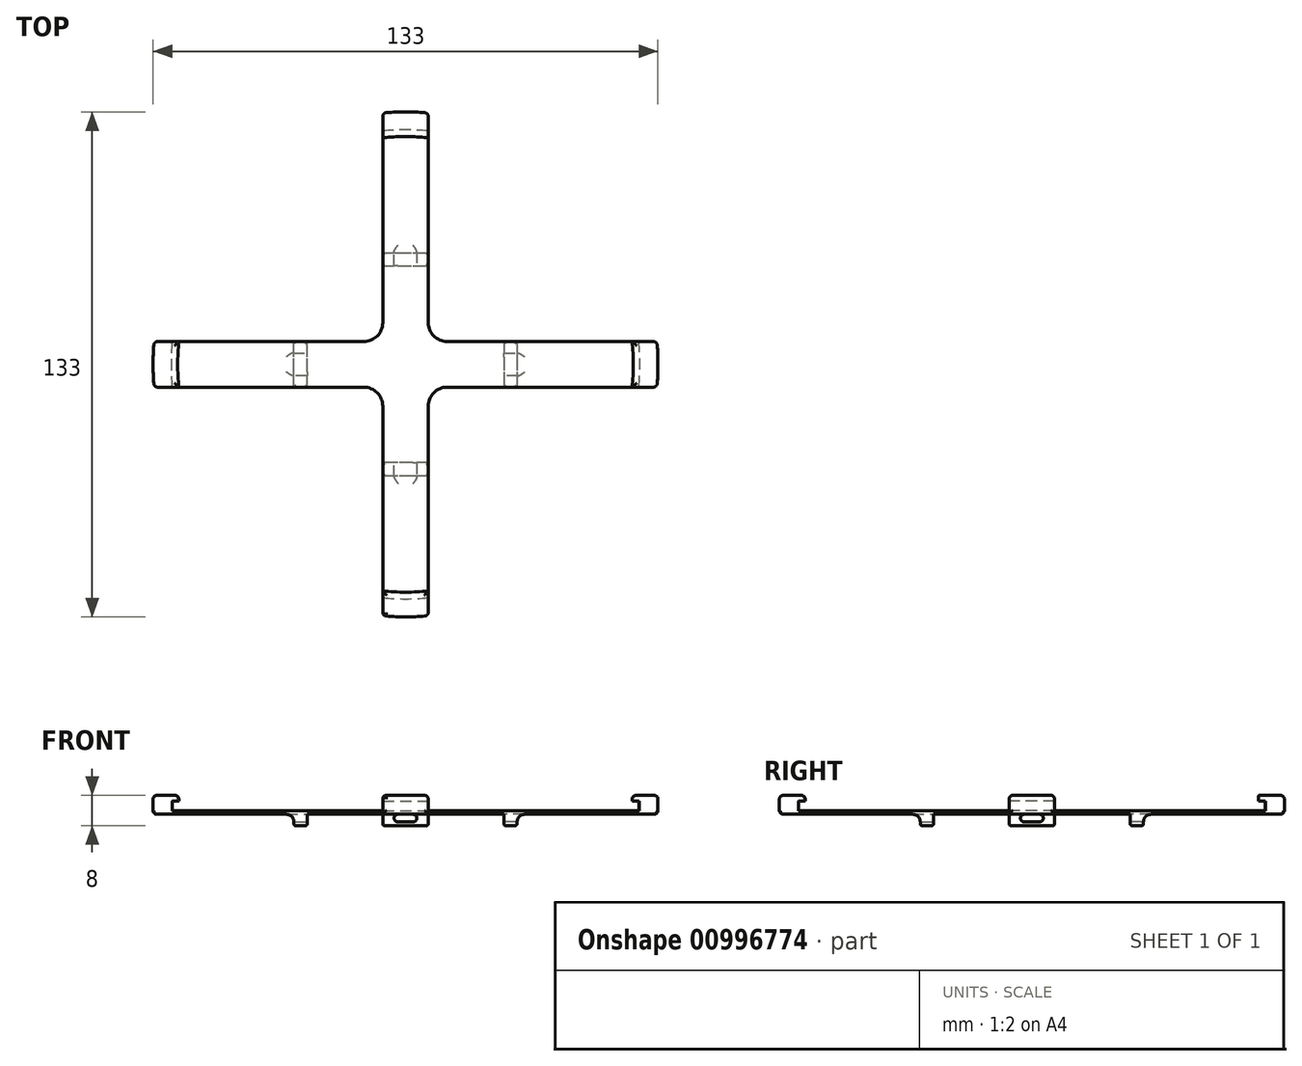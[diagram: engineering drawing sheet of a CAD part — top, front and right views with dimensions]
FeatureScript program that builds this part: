
annotation { "Feature Type Name" : "Feature", "Feature Type Description" : "" }
export const myFeature = defineFeature(function(context is Context, id is Id, definition is map)
    precondition{}
    {
        {
            var Q0;
            Q0=qCreatedBy(makeId("Top.planeOp"),FACE);
            var sketch = newSketch(context, id + "F0", { "sketchPlane" : qUnion([Q0])});
            skCircle(sketch, "E0", {"center": v(0, 0) * mm, "radius": 66.5 * mm, "construction": true});
            skLineSegment(sketch, "E1.bottom", {"start": v(6, -6) * mm, "end": v(-6, -6) * mm, "construction": true});
            skLineSegment(sketch, "E1.top", {"start": v(6, 6) * mm, "end": v(-6, 6) * mm, "construction": true});
            skLineSegment(sketch, "E1.left", {"start": v(6, -6) * mm, "end": v(6, 6) * mm, "construction": true});
            skLineSegment(sketch, "E1.right", {"start": v(-6, -6) * mm, "end": v(-6, 6) * mm, "construction": true});
            skLineSegment(sketch, "E2", {"start": v(-6, 6) * mm, "end": v(-66.23, 6) * mm});
            skLineSegment(sketch, "E3", {"start": v(-6, -6) * mm, "end": v(-66.23, -6) * mm});
            skArc(sketch, "E4", {"start": v(-66.23, 6) * mm, "mid": v(-66.5, 0) * mm, "end": v(-66.23, -6) * mm});
            skLineSegment(sketch, "E5.1.0", {"start": v(-6, -6) * mm, "end": v(-6, -66.23) * mm});
            skLineSegment(sketch, "E5.1.1", {"start": v(6, -6) * mm, "end": v(6, -66.23) * mm});
            skArc(sketch, "E5.1.2", {"start": v(-6, -66.23) * mm, "mid": v(0, -66.5) * mm, "end": v(6, -66.23) * mm});
            skLineSegment(sketch, "E5.2.0", {"start": v(6, -6) * mm, "end": v(66.23, -6) * mm});
            skLineSegment(sketch, "E5.2.1", {"start": v(6, 6) * mm, "end": v(66.23, 6) * mm});
            skArc(sketch, "E5.2.2", {"start": v(66.23, -6) * mm, "mid": v(66.5, 0) * mm, "end": v(66.23, 6) * mm});
            skLineSegment(sketch, "E5.3.0", {"start": v(6, 6) * mm, "end": v(6, 66.23) * mm});
            skLineSegment(sketch, "E5.3.1", {"start": v(-6, 6) * mm, "end": v(-6, 66.23) * mm});
            skArc(sketch, "E5.3.2", {"start": v(6, 66.23) * mm, "mid": v(0, 66.5) * mm, "end": v(-6, 66.23) * mm});
            skSolve(sketch);
        }
        {
            var Q0;
            Q0 = qSketchRegion(id + "F0", true);
            extrude(context, id + "F1", {"entities" : qUnion([Q0]), "depth" : 5 * mm, "offsetDistance" : 25 * mm});
        }
        {
            var Q0;
            Q0=makeQuery(id+"F1.opExtrude","CAP_FACE",FACE,{"disambiguationData":[OSD([sQuery(id+"F0.wireOp",EDGE,"E2"),sQuery(id+"F0.wireOp",EDGE,"E3"),sQuery(id+"F0.wireOp",EDGE,"E4"),sQuery(id+"F0.wireOp",EDGE,"E5.1.0"),sQuery(id+"F0.wireOp",EDGE,"E5.1.1"),sQuery(id+"F0.wireOp",EDGE,"E5.1.2"),sQuery(id+"F0.wireOp",EDGE,"E5.2.0"),sQuery(id+"F0.wireOp",EDGE,"E5.2.1"),sQuery(id+"F0.wireOp",EDGE,"E5.2.2"),sQuery(id+"F0.wireOp",EDGE,"E5.3.0"),sQuery(id+"F0.wireOp",EDGE,"E5.3.1"),sQuery(id+"F0.wireOp",EDGE,"E5.3.2")])],"isStart":false});
            var sketch = newSketch(context, id + "F2", { "sketchPlane" : qUnion([Q0])});
            skCircle(sketch, "E6", {"center": v(0, 0) * mm, "radius": 60 * mm, "construction": true});
            skArc(sketch, "E7", {"start": v(-59.7, 6) * mm, "mid": v(-60, 0) * mm, "end": v(-59.7, -6) * mm});
            skLineSegment(sketch, "E8", {"start": v(-59.7, 6) * mm, "end": v(-6, 6) * mm});
            skLineSegment(sketch, "E9", {"start": v(-59.7, -6) * mm, "end": v(-6, -6) * mm});
            skLineSegment(sketch, "E10.1.0", {"start": v(6, -59.7) * mm, "end": v(6, -6) * mm});
            skArc(sketch, "E10.1.1", {"start": v(-6, -59.7) * mm, "mid": v(0, -60) * mm, "end": v(6, -59.7) * mm});
            skLineSegment(sketch, "E10.1.2", {"start": v(-6, -59.7) * mm, "end": v(-6, -6) * mm});
            skLineSegment(sketch, "E10.2.0", {"start": v(59.7, 6) * mm, "end": v(6, 6) * mm});
            skArc(sketch, "E10.2.1", {"start": v(59.7, -6) * mm, "mid": v(60, 0) * mm, "end": v(59.7, 6) * mm});
            skLineSegment(sketch, "E10.2.2", {"start": v(59.7, -6) * mm, "end": v(6, -6) * mm});
            skLineSegment(sketch, "E10.3.0", {"start": v(-6, 59.7) * mm, "end": v(-6, 6) * mm});
            skArc(sketch, "E10.3.1", {"start": v(6, 59.7) * mm, "mid": v(0, 60) * mm, "end": v(-6, 59.7) * mm});
            skLineSegment(sketch, "E10.3.2", {"start": v(6, 59.7) * mm, "end": v(6, 6) * mm});
            skSolve(sketch);
        }
        {
            var Q0;
            Q0 = qSketchRegion(id + "F2", true);
            extrude(context, id + "F3", {"entities" : qUnion([Q0]), "operationType" : NewBodyOperationType.REMOVE, "oppositeDirection" : true, "depth" : 4 * mm, "offsetDistance" : 25 * mm});
        }
        {
            var Q0;
            Q0=makeQuery(id+"F3.boolean.opBoolean","COPY",FACE,{"derivedFrom":makeQuery(id+"F3.opExtrude","CAP_FACE",FACE,{"disambiguationData":[OSD([sQuery(id+"F2.wireOp",EDGE,"E7"),sQuery(id+"F2.wireOp",EDGE,"E8"),sQuery(id+"F2.wireOp",EDGE,"E9"),sQuery(id+"F2.wireOp",EDGE,"E10.1.0"),sQuery(id+"F2.wireOp",EDGE,"E10.1.1"),sQuery(id+"F2.wireOp",EDGE,"E10.1.2"),sQuery(id+"F2.wireOp",EDGE,"E10.2.0"),sQuery(id+"F2.wireOp",EDGE,"E10.2.1"),sQuery(id+"F2.wireOp",EDGE,"E10.2.2"),sQuery(id+"F2.wireOp",EDGE,"E10.3.0"),sQuery(id+"F2.wireOp",EDGE,"E10.3.1"),sQuery(id+"F2.wireOp",EDGE,"E10.3.2")])],"isStart":false})});
            var sketch = newSketch(context, id + "F4", { "sketchPlane" : qUnion([Q0])});
            skLineSegment(sketch, "E11.bottom", {"start": v(-6, 6) * mm, "end": v(-64.12, 6) * mm, "construction": true});
            skLineSegment(sketch, "E11.top", {"start": v(-6, -6) * mm, "end": v(-64.12, -6) * mm, "construction": true});
            skLineSegment(sketch, "E11.left", {"start": v(-6, 6) * mm, "end": v(-6, -6) * mm, "construction": true});
            skLineSegment(sketch, "E11.right", {"start": v(-64.12, 6) * mm, "end": v(-64.12, -6) * mm, "construction": true});
            skArc(sketch, "E12", {"start": v(-61.46, 6) * mm, "mid": v(-61.75, 0) * mm, "end": v(-61.46, -6) * mm});
            skLineSegment(sketch, "E13", {"start": v(-61.46, 6) * mm, "end": v(-6, 6) * mm});
            skLineSegment(sketch, "E14", {"start": v(-6, -6) * mm, "end": v(-61.46, -6) * mm});
            skLineSegment(sketch, "E15.1.0", {"start": v(6, -6) * mm, "end": v(6, -61.46) * mm});
            skLineSegment(sketch, "E15.1.1", {"start": v(-6, -61.46) * mm, "end": v(-6, -6) * mm});
            skArc(sketch, "E15.1.2", {"start": v(-6, -61.46) * mm, "mid": v(0, -61.75) * mm, "end": v(6, -61.46) * mm});
            skLineSegment(sketch, "E15.2.0", {"start": v(6, 6) * mm, "end": v(61.46, 6) * mm});
            skLineSegment(sketch, "E15.2.1", {"start": v(61.46, -6) * mm, "end": v(6, -6) * mm});
            skArc(sketch, "E15.2.2", {"start": v(61.46, -6) * mm, "mid": v(61.75, 0) * mm, "end": v(61.46, 6) * mm});
            skLineSegment(sketch, "E15.3.0", {"start": v(-6, 6) * mm, "end": v(-6, 61.46) * mm});
            skLineSegment(sketch, "E15.3.1", {"start": v(6, 61.46) * mm, "end": v(6, 6) * mm});
            skArc(sketch, "E15.3.2", {"start": v(6, 61.46) * mm, "mid": v(0, 61.75) * mm, "end": v(-6, 61.46) * mm});
            skPoint(sketch, "E15.center", {"position": v(0, 0) * mm});
            skSolve(sketch);
        }
        {
            var Q0;
            Q0 = qSketchRegion(id + "F4", true);
            extrude(context, id + "F5", {"entities" : qUnion([Q0]), "operationType" : NewBodyOperationType.REMOVE, "depth" : 2.5 * mm, "offsetDistance" : 25 * mm});
        }
        {
            var Q0;
            Q0=makeQuery(id+"F1.opExtrude","SWEPT_EDGE",EDGE,{"disambiguationData":[OSD([sQuery(id+"F0.wireOp",EDGE,"E5.1.1"),sQuery(id+"F0.wireOp",EDGE,"E5.2.0")])]});
            var Q1;
            Q1=makeQuery(id+"F1.opExtrude","SWEPT_EDGE",EDGE,{"disambiguationData":[OSD([sQuery(id+"F0.wireOp",EDGE,"E3"),sQuery(id+"F0.wireOp",EDGE,"E5.1.0")])]});
            var Q2;
            Q2=makeQuery(id+"F1.opExtrude","SWEPT_EDGE",EDGE,{"disambiguationData":[OSD([sQuery(id+"F0.wireOp",EDGE,"E2"),sQuery(id+"F0.wireOp",EDGE,"E5.3.1")])]});
            var Q3;
            Q3=makeQuery(id+"F1.opExtrude","SWEPT_EDGE",EDGE,{"disambiguationData":[OSD([sQuery(id+"F0.wireOp",EDGE,"E5.2.1"),sQuery(id+"F0.wireOp",EDGE,"E5.3.0")])]});
            fillet(context, id + "F6", {"entities" : qUnion([Q0, Q1, Q2, Q3]), "radius" : 5 * mm, "tangentPropagation" : true, "allowEdgeOverflow" : false});
        }
        {
            var Q0;
            Q0=makeQuery(id+"F1.opExtrude","CAP_EDGE",EDGE,{"disambiguationData":[OSD([sQuery(id+"F0.wireOp",EDGE,"E5.3.2")])],"isStart":false});
            var Q1;
            Q1=makeQuery(id+"F3.boolean.opBoolean","COPY",EDGE,{"derivedFrom":makeQuery(id+"F3.opExtrude","CAP_EDGE",EDGE,{"disambiguationData":[OSD([sQuery(id+"F2.wireOp",EDGE,"E10.3.1")])],"isStart":true})});
            var Q2;
            Q2=makeQuery(id+"F1.opExtrude","SWEPT_EDGE",EDGE,{"disambiguationData":[OSD([sQuery(id+"F0.wireOp",EDGE,"E5.3.0"),sQuery(id+"F0.wireOp",EDGE,"E5.3.2")])]});
            var Q3;
            Q3=makeQuery(id+"F1.opExtrude","CAP_EDGE",EDGE,{"disambiguationData":[OSD([sQuery(id+"F0.wireOp",EDGE,"E5.3.0")])],"isStart":false});
            var Q4;
            Q4=makeQuery(id+"F1.opExtrude","CAP_EDGE",EDGE,{"disambiguationData":[OSD([sQuery(id+"F0.wireOp",EDGE,"E5.3.1")])],"isStart":false});
            var Q5;
            Q5=makeQuery(id+"F1.opExtrude","SWEPT_EDGE",EDGE,{"disambiguationData":[OSD([sQuery(id+"F0.wireOp",EDGE,"E5.3.1"),sQuery(id+"F0.wireOp",EDGE,"E5.3.2")])]});
            var Q6;
            Q6=makeQuery(id+"F1.opExtrude","CAP_EDGE",EDGE,{"disambiguationData":[OSD([sQuery(id+"F0.wireOp",EDGE,"E5.3.2")])],"isStart":true});
            var Q7;
            Q7=makeQuery(id+"F1.opExtrude","CAP_EDGE",EDGE,{"disambiguationData":[OSD([sQuery(id+"F0.wireOp",EDGE,"E2")])],"isStart":false});
            var Q8;
            Q8=makeQuery(id+"F3.boolean.opBoolean","COPY",EDGE,{"derivedFrom":makeQuery(id+"F3.opExtrude","CAP_EDGE",EDGE,{"disambiguationData":[OSD([sQuery(id+"F2.wireOp",EDGE,"E7")])],"isStart":true})});
            var Q9;
            Q9=makeQuery(id+"F1.opExtrude","CAP_EDGE",EDGE,{"disambiguationData":[OSD([sQuery(id+"F0.wireOp",EDGE,"E3")])],"isStart":false});
            var Q10;
            Q10=makeQuery(id+"F1.opExtrude","CAP_EDGE",EDGE,{"disambiguationData":[OSD([sQuery(id+"F0.wireOp",EDGE,"E4")])],"isStart":false});
            var Q11;
            Q11=makeQuery(id+"F1.opExtrude","SWEPT_EDGE",EDGE,{"disambiguationData":[OSD([sQuery(id+"F0.wireOp",EDGE,"E3"),sQuery(id+"F0.wireOp",EDGE,"E4")])]});
            var Q12;
            Q12=makeQuery(id+"F1.opExtrude","SWEPT_EDGE",EDGE,{"disambiguationData":[OSD([sQuery(id+"F0.wireOp",EDGE,"E2"),sQuery(id+"F0.wireOp",EDGE,"E4")])]});
            var Q13;
            Q13=makeQuery(id+"F1.opExtrude","SWEPT_EDGE",EDGE,{"disambiguationData":[OSD([sQuery(id+"F0.wireOp",EDGE,"E5.1.0"),sQuery(id+"F0.wireOp",EDGE,"E5.1.2")])]});
            var Q14;
            Q14=makeQuery(id+"F1.opExtrude","CAP_EDGE",EDGE,{"disambiguationData":[OSD([sQuery(id+"F0.wireOp",EDGE,"E5.1.2")])],"isStart":false});
            var Q15;
            Q15=makeQuery(id+"F1.opExtrude","SWEPT_EDGE",EDGE,{"disambiguationData":[OSD([sQuery(id+"F0.wireOp",EDGE,"E5.1.1"),sQuery(id+"F0.wireOp",EDGE,"E5.1.2")])]});
            var Q16;
            Q16=makeQuery(id+"F3.boolean.opBoolean","COPY",EDGE,{"derivedFrom":makeQuery(id+"F3.opExtrude","CAP_EDGE",EDGE,{"disambiguationData":[OSD([sQuery(id+"F2.wireOp",EDGE,"E10.1.1")])],"isStart":true})});
            var Q17;
            Q17=makeQuery(id+"F1.opExtrude","CAP_EDGE",EDGE,{"disambiguationData":[OSD([sQuery(id+"F0.wireOp",EDGE,"E5.1.1")])],"isStart":false});
            var Q18;
            Q18=makeQuery(id+"F1.opExtrude","CAP_EDGE",EDGE,{"disambiguationData":[OSD([sQuery(id+"F0.wireOp",EDGE,"E5.1.0")])],"isStart":false});
            var Q19;
            Q19=makeQuery(id+"F1.opExtrude","SWEPT_EDGE",EDGE,{"disambiguationData":[OSD([sQuery(id+"F0.wireOp",EDGE,"E5.2.1"),sQuery(id+"F0.wireOp",EDGE,"E5.2.2")])]});
            var Q20;
            Q20=makeQuery(id+"F1.opExtrude","CAP_EDGE",EDGE,{"disambiguationData":[OSD([sQuery(id+"F0.wireOp",EDGE,"E5.2.2")])],"isStart":true});
            var Q21;
            Q21=makeQuery(id+"F1.opExtrude","CAP_EDGE",EDGE,{"disambiguationData":[OSD([sQuery(id+"F0.wireOp",EDGE,"E5.2.2")])],"isStart":false});
            var Q22;
            Q22=makeQuery(id+"F1.opExtrude","SWEPT_EDGE",EDGE,{"disambiguationData":[OSD([sQuery(id+"F0.wireOp",EDGE,"E5.2.0"),sQuery(id+"F0.wireOp",EDGE,"E5.2.2")])]});
            var Q23;
            Q23=makeQuery(id+"F1.opExtrude","CAP_EDGE",EDGE,{"disambiguationData":[OSD([sQuery(id+"F0.wireOp",EDGE,"E5.2.1")])],"isStart":false});
            var Q24;
            Q24=makeQuery(id+"F3.boolean.opBoolean","COPY",EDGE,{"derivedFrom":makeQuery(id+"F3.opExtrude","CAP_EDGE",EDGE,{"disambiguationData":[OSD([sQuery(id+"F2.wireOp",EDGE,"E10.2.1")])],"isStart":true})});
            var Q25;
            Q25=makeQuery(id+"F1.opExtrude","CAP_EDGE",EDGE,{"disambiguationData":[OSD([sQuery(id+"F0.wireOp",EDGE,"E5.2.0")])],"isStart":false});
            var Q26;
            Q26=makeQuery(id+"F1.opExtrude","CAP_EDGE",EDGE,{"disambiguationData":[OSD([sQuery(id+"F0.wireOp",EDGE,"E4")])],"isStart":true});
            var Q27;
            Q27=makeQuery(id+"F1.opExtrude","CAP_EDGE",EDGE,{"disambiguationData":[OSD([sQuery(id+"F0.wireOp",EDGE,"E5.1.2")])],"isStart":true});
            fillet(context, id + "F7", {"entities" : qUnion([Q0, Q1, Q2, Q3, Q4, Q5, Q6, Q7, Q8, Q9, Q10, Q11, Q12, Q13, Q14, Q15, Q16, Q17, Q18, Q19, Q20, Q21, Q22, Q23, Q24, Q25, Q26, Q27]), "radius" : 1 * mm, "tangentPropagation" : true, "allowEdgeOverflow" : false});
        }
        {
            var Q0;
            Q0=makeQuery(id+"F1.opExtrude","CAP_FACE",FACE,{"disambiguationData":[OSD([sQuery(id+"F0.wireOp",EDGE,"E2"),sQuery(id+"F0.wireOp",EDGE,"E3"),sQuery(id+"F0.wireOp",EDGE,"E4"),sQuery(id+"F0.wireOp",EDGE,"E5.1.0"),sQuery(id+"F0.wireOp",EDGE,"E5.1.1"),sQuery(id+"F0.wireOp",EDGE,"E5.1.2"),sQuery(id+"F0.wireOp",EDGE,"E5.2.0"),sQuery(id+"F0.wireOp",EDGE,"E5.2.1"),sQuery(id+"F0.wireOp",EDGE,"E5.2.2"),sQuery(id+"F0.wireOp",EDGE,"E5.3.0"),sQuery(id+"F0.wireOp",EDGE,"E5.3.1"),sQuery(id+"F0.wireOp",EDGE,"E5.3.2")])],"isStart":true});
            var sketch = newSketch(context, id + "F8", { "sketchPlane" : qUnion([Q0])});
            skCircle(sketch, "E16", {"center": v(0, 0) * mm, "radius": 30 * mm, "construction": true});
            skLineSegment(sketch, "E17", {"start": v(0, 0) * mm, "end": v(-65.5, 0) * mm, "construction": true});
            skLineSegment(sketch, "E18.bottom", {"start": v(-29.4, 6) * mm, "end": v(-25.9, 6) * mm});
            skLineSegment(sketch, "E18.top", {"start": v(-29.4, -6) * mm, "end": v(-25.9, -6) * mm});
            skLineSegment(sketch, "E18.left", {"start": v(-29.4, 6) * mm, "end": v(-29.4, -6) * mm});
            skLineSegment(sketch, "E18.right", {"start": v(-25.9, 6) * mm, "end": v(-25.9, -6) * mm});
            skLineSegment(sketch, "E19.1.0", {"start": v(-6, -29.4) * mm, "end": v(-6, -25.9) * mm});
            skLineSegment(sketch, "E19.1.1", {"start": v(-6, -25.9) * mm, "end": v(6, -25.9) * mm});
            skLineSegment(sketch, "E19.1.2", {"start": v(6, -29.4) * mm, "end": v(6, -25.9) * mm});
            skLineSegment(sketch, "E19.1.3", {"start": v(-6, -29.4) * mm, "end": v(6, -29.4) * mm});
            skLineSegment(sketch, "E19.2.0", {"start": v(29.4, -6) * mm, "end": v(25.9, -6) * mm});
            skLineSegment(sketch, "E19.2.1", {"start": v(25.9, -6) * mm, "end": v(25.9, 6) * mm});
            skLineSegment(sketch, "E19.2.2", {"start": v(29.4, 6) * mm, "end": v(25.9, 6) * mm});
            skLineSegment(sketch, "E19.2.3", {"start": v(29.4, -6) * mm, "end": v(29.4, 6) * mm});
            skLineSegment(sketch, "E19.3.0", {"start": v(6, 29.4) * mm, "end": v(6, 25.9) * mm});
            skLineSegment(sketch, "E19.3.1", {"start": v(6, 25.9) * mm, "end": v(-6, 25.9) * mm});
            skLineSegment(sketch, "E19.3.2", {"start": v(-6, 29.4) * mm, "end": v(-6, 25.9) * mm});
            skLineSegment(sketch, "E19.3.3", {"start": v(6, 29.4) * mm, "end": v(-6, 29.4) * mm});
            skSolve(sketch);
        }
        {
            var Q0;
            Q0 = qSketchRegion(id + "F8", true);
            extrude(context, id + "F9", {"entities" : qUnion([Q0]), "operationType" : NewBodyOperationType.ADD, "depth" : 3 * mm, "offsetDistance" : 25 * mm});
        }
        {
            var Q0;
            {var subQ0=sQuery(id+"F0.wireOp",EDGE,"E5.3.0");var subQ1=sQuery(id+"F0.wireOp",EDGE,"E5.2.1");var subQ2=sQuery(id+"F0.wireOp",EDGE,"E5.2.0");var subQ3=sQuery(id+"F0.wireOp",EDGE,"E5.1.1");var subQ4=sQuery(id+"F0.wireOp",EDGE,"E5.1.0");var subQ5=sQuery(id+"F0.wireOp",EDGE,"E3");var subQ6=sQuery(id+"F0.wireOp",EDGE,"E2");var subQ7=sQuery(id+"F0.wireOp",EDGE,"E5.3.1");Q0=makeQuery(id+"F9.boolean.opBoolean","SPLIT",FACE,{"disambiguationData":[TD([makeQuery(id+"F9.opExtrude","SWEPT_FACE",FACE,{"disambiguationData":[OSD([sQuery(id+"F8.wireOp",EDGE,"E18.right")])]})])],"derivedFrom":makeQuery(id+"F1.opExtrude","CAP_FACE",FACE,{"disambiguationData":[OSD([subQ6,subQ5,sQuery(id+"F0.wireOp",EDGE,"E4"),subQ4,subQ3,sQuery(id+"F0.wireOp",EDGE,"E5.1.2"),subQ2,subQ1,sQuery(id+"F0.wireOp",EDGE,"E5.2.2"),subQ0,subQ7,sQuery(id+"F0.wireOp",EDGE,"E5.3.2")])],"isStart":true})});}
            var sketch = newSketch(context, id + "F10", { "sketchPlane" : qUnion([Q0])});
            skLineSegment(sketch, "E20", {"start": v(0, 0) * mm, "end": v(-61.83, 0) * mm, "construction": true});
            skLineSegment(sketch, "E21.0", {"start": v(0, 3) * mm, "end": v(-61.83, 3) * mm, "construction": true});
            skLineSegment(sketch, "E22.0", {"start": v(0, -3) * mm, "end": v(-61.83, -3) * mm, "construction": true});
            skLineSegment(sketch, "E23.bottom", {"start": v(-30.91, 3) * mm, "end": v(-23.73, 3) * mm});
            skLineSegment(sketch, "E23.top", {"start": v(-30.91, -3) * mm, "end": v(-23.73, -3) * mm});
            skLineSegment(sketch, "E23.left", {"start": v(-30.91, 3) * mm, "end": v(-30.91, -3) * mm});
            skLineSegment(sketch, "E23.right", {"start": v(-23.73, 3) * mm, "end": v(-23.73, -3) * mm});
            skLineSegment(sketch, "E24.1.0", {"start": v(-3, -30.91) * mm, "end": v(-3, -23.73) * mm});
            skLineSegment(sketch, "E24.1.1", {"start": v(3, -30.91) * mm, "end": v(3, -23.73) * mm});
            skLineSegment(sketch, "E24.1.2", {"start": v(-3, -23.73) * mm, "end": v(3, -23.73) * mm});
            skLineSegment(sketch, "E24.1.3", {"start": v(-3, -30.91) * mm, "end": v(3, -30.91) * mm});
            skLineSegment(sketch, "E24.2.0", {"start": v(30.91, -3) * mm, "end": v(23.73, -3) * mm});
            skLineSegment(sketch, "E24.2.1", {"start": v(30.91, 3) * mm, "end": v(23.73, 3) * mm});
            skLineSegment(sketch, "E24.2.2", {"start": v(23.73, -3) * mm, "end": v(23.73, 3) * mm});
            skLineSegment(sketch, "E24.2.3", {"start": v(30.91, -3) * mm, "end": v(30.91, 3) * mm});
            skLineSegment(sketch, "E24.3.0", {"start": v(3, 30.91) * mm, "end": v(3, 23.73) * mm});
            skLineSegment(sketch, "E24.3.1", {"start": v(-3, 30.91) * mm, "end": v(-3, 23.73) * mm});
            skLineSegment(sketch, "E24.3.2", {"start": v(3, 23.73) * mm, "end": v(-3, 23.73) * mm});
            skLineSegment(sketch, "E24.3.3", {"start": v(3, 30.91) * mm, "end": v(-3, 30.91) * mm});
            skPoint(sketch, "E24.center", {"position": v(0, 0) * mm});
            skSolve(sketch);
        }
        {
            var Q0;
            Q0 = qSketchRegion(id + "F10", true);
            extrude(context, id + "F11", {"entities" : qUnion([Q0]), "operationType" : NewBodyOperationType.REMOVE, "depth" : 2 * mm, "offsetDistance" : 25 * mm});
        }
        {
            var Q0;
            {var subQ0=sQuery(id+"F8.wireOp",EDGE,"E18.left");var subQ1=sQuery(id+"F0.wireOp",EDGE,"E3");Q0=makeQuery(id+"F11.boolean.opBoolean","SPLIT",EDGE,{"disambiguationData":[TD([makeQuery(id+"F1.opExtrude","SWEPT_FACE",FACE,{"disambiguationData":[OSD([subQ1])]})])],"derivedFrom":makeQuery(id+"F9.opExtrude","CAP_EDGE",EDGE,{"disambiguationData":[OSD([subQ0])],"isStart":true})});}
            var Q1;
            {var subQ0=sQuery(id+"F8.wireOp",EDGE,"E18.left");var subQ1=sQuery(id+"F0.wireOp",EDGE,"E2");Q1=makeQuery(id+"F11.boolean.opBoolean","SPLIT",EDGE,{"disambiguationData":[TD([makeQuery(id+"F1.opExtrude","SWEPT_FACE",FACE,{"disambiguationData":[OSD([subQ1])]})])],"derivedFrom":makeQuery(id+"F9.opExtrude","CAP_EDGE",EDGE,{"disambiguationData":[OSD([subQ0])],"isStart":true})});}
            var Q2;
            {var subQ0=sQuery(id+"F0.wireOp",EDGE,"E2");var subQ1=sQuery(id+"F8.wireOp",EDGE,"E18.right");Q2=makeQuery(id+"F11.boolean.opBoolean","SPLIT",EDGE,{"disambiguationData":[TD([makeQuery(id+"F1.opExtrude","SWEPT_FACE",FACE,{"disambiguationData":[OSD([subQ0])]})])],"derivedFrom":makeQuery(id+"F9.opExtrude","CAP_EDGE",EDGE,{"disambiguationData":[OSD([subQ1])],"isStart":true})});}
            var Q3;
            {var subQ0=sQuery(id+"F8.wireOp",EDGE,"E18.right");var subQ2=sQuery(id+"F0.wireOp",EDGE,"E3");Q3=makeQuery(id+"F11.boolean.opBoolean","SPLIT",EDGE,{"disambiguationData":[TD([makeQuery(id+"F1.opExtrude","SWEPT_FACE",FACE,{"disambiguationData":[OSD([subQ2])]})])],"derivedFrom":makeQuery(id+"F9.opExtrude","CAP_EDGE",EDGE,{"disambiguationData":[OSD([subQ0])],"isStart":true})});}
            var Q4;
            {var subQ0=sQuery(id+"F8.wireOp",EDGE,"E19.2.3");var subQ2=sQuery(id+"F0.wireOp",EDGE,"E5.2.1");Q4=makeQuery(id+"F11.boolean.opBoolean","SPLIT",EDGE,{"disambiguationData":[TD([makeQuery(id+"F1.opExtrude","SWEPT_FACE",FACE,{"disambiguationData":[OSD([subQ2])]})])],"derivedFrom":makeQuery(id+"F9.opExtrude","CAP_EDGE",EDGE,{"disambiguationData":[OSD([subQ0])],"isStart":true})});}
            var Q5;
            {var subQ0=sQuery(id+"F8.wireOp",EDGE,"E19.2.3");var subQ1=sQuery(id+"F0.wireOp",EDGE,"E5.2.0");Q5=makeQuery(id+"F11.boolean.opBoolean","SPLIT",EDGE,{"disambiguationData":[TD([makeQuery(id+"F1.opExtrude","SWEPT_FACE",FACE,{"disambiguationData":[OSD([subQ1])]})])],"derivedFrom":makeQuery(id+"F9.opExtrude","CAP_EDGE",EDGE,{"disambiguationData":[OSD([subQ0])],"isStart":true})});}
            var Q6;
            {var subQ0=sQuery(id+"F8.wireOp",EDGE,"E19.2.1");var subQ1=sQuery(id+"F0.wireOp",EDGE,"E5.2.1");Q6=makeQuery(id+"F11.boolean.opBoolean","SPLIT",EDGE,{"disambiguationData":[TD([makeQuery(id+"F1.opExtrude","SWEPT_FACE",FACE,{"disambiguationData":[OSD([subQ1])]})])],"derivedFrom":makeQuery(id+"F9.opExtrude","CAP_EDGE",EDGE,{"disambiguationData":[OSD([subQ0])],"isStart":true})});}
            var Q7;
            {var subQ0=sQuery(id+"F8.wireOp",EDGE,"E19.2.1");var subQ1=sQuery(id+"F0.wireOp",EDGE,"E5.2.0");Q7=makeQuery(id+"F11.boolean.opBoolean","SPLIT",EDGE,{"disambiguationData":[TD([makeQuery(id+"F1.opExtrude","SWEPT_FACE",FACE,{"disambiguationData":[OSD([subQ1])]})])],"derivedFrom":makeQuery(id+"F9.opExtrude","CAP_EDGE",EDGE,{"disambiguationData":[OSD([subQ0])],"isStart":true})});}
            var Q8;
            {var subQ0=sQuery(id+"F0.wireOp",EDGE,"E5.1.1");var subQ1=sQuery(id+"F8.wireOp",EDGE,"E19.3.1");Q8=makeQuery(id+"F11.boolean.opBoolean","SPLIT",EDGE,{"disambiguationData":[TD([makeQuery(id+"F1.opExtrude","SWEPT_FACE",FACE,{"disambiguationData":[OSD([subQ0])]})])],"derivedFrom":makeQuery(id+"F9.opExtrude","CAP_EDGE",EDGE,{"disambiguationData":[OSD([subQ1])],"isStart":true})});}
            var Q9;
            {var subQ0=sQuery(id+"F0.wireOp",EDGE,"E5.1.0");var subQ1=sQuery(id+"F8.wireOp",EDGE,"E19.3.1");Q9=makeQuery(id+"F11.boolean.opBoolean","SPLIT",EDGE,{"disambiguationData":[TD([makeQuery(id+"F1.opExtrude","SWEPT_FACE",FACE,{"disambiguationData":[OSD([subQ0])]})])],"derivedFrom":makeQuery(id+"F9.opExtrude","CAP_EDGE",EDGE,{"disambiguationData":[OSD([subQ1])],"isStart":true})});}
            var Q10;
            {var subQ0=sQuery(id+"F0.wireOp",EDGE,"E5.3.1");var subQ1=sQuery(id+"F8.wireOp",EDGE,"E19.1.3");Q10=makeQuery(id+"F11.boolean.opBoolean","SPLIT",EDGE,{"disambiguationData":[TD([makeQuery(id+"F1.opExtrude","SWEPT_FACE",FACE,{"disambiguationData":[OSD([subQ0])]})])],"derivedFrom":makeQuery(id+"F9.opExtrude","CAP_EDGE",EDGE,{"disambiguationData":[OSD([subQ1])],"isStart":true})});}
            var Q11;
            {var subQ0=sQuery(id+"F8.wireOp",EDGE,"E19.1.3");var subQ1=sQuery(id+"F0.wireOp",EDGE,"E5.3.0");Q11=makeQuery(id+"F11.boolean.opBoolean","SPLIT",EDGE,{"disambiguationData":[TD([makeQuery(id+"F1.opExtrude","SWEPT_FACE",FACE,{"disambiguationData":[OSD([subQ1])]})])],"derivedFrom":makeQuery(id+"F9.opExtrude","CAP_EDGE",EDGE,{"disambiguationData":[OSD([subQ0])],"isStart":true})});}
            var Q12;
            {var subQ0=sQuery(id+"F8.wireOp",EDGE,"E19.1.1");var subQ1=sQuery(id+"F0.wireOp",EDGE,"E5.3.0");Q12=makeQuery(id+"F11.boolean.opBoolean","SPLIT",EDGE,{"disambiguationData":[TD([makeQuery(id+"F1.opExtrude","SWEPT_FACE",FACE,{"disambiguationData":[OSD([subQ1])]})])],"derivedFrom":makeQuery(id+"F9.opExtrude","CAP_EDGE",EDGE,{"disambiguationData":[OSD([subQ0])],"isStart":true})});}
            var Q13;
            {var subQ0=sQuery(id+"F8.wireOp",EDGE,"E19.1.1");var subQ1=sQuery(id+"F0.wireOp",EDGE,"E5.3.1");Q13=makeQuery(id+"F11.boolean.opBoolean","SPLIT",EDGE,{"disambiguationData":[TD([makeQuery(id+"F1.opExtrude","SWEPT_FACE",FACE,{"disambiguationData":[OSD([subQ1])]})])],"derivedFrom":makeQuery(id+"F9.opExtrude","CAP_EDGE",EDGE,{"disambiguationData":[OSD([subQ0])],"isStart":true})});}
            var Q14;
            {var subQ0=sQuery(id+"F8.wireOp",EDGE,"E19.3.3");var subQ1=sQuery(id+"F0.wireOp",EDGE,"E5.1.1");Q14=makeQuery(id+"F11.boolean.opBoolean","SPLIT",EDGE,{"disambiguationData":[TD([makeQuery(id+"F1.opExtrude","SWEPT_FACE",FACE,{"disambiguationData":[OSD([subQ1])]})])],"derivedFrom":makeQuery(id+"F9.opExtrude","CAP_EDGE",EDGE,{"disambiguationData":[OSD([subQ0])],"isStart":true})});}
            var Q15;
            {var subQ0=sQuery(id+"F8.wireOp",EDGE,"E19.3.3");var subQ1=sQuery(id+"F0.wireOp",EDGE,"E5.1.0");Q15=makeQuery(id+"F11.boolean.opBoolean","SPLIT",EDGE,{"disambiguationData":[TD([makeQuery(id+"F1.opExtrude","SWEPT_FACE",FACE,{"disambiguationData":[OSD([subQ1])]})])],"derivedFrom":makeQuery(id+"F9.opExtrude","CAP_EDGE",EDGE,{"disambiguationData":[OSD([subQ0])],"isStart":true})});}
            fillet(context, id + "F12", {"entities" : qUnion([Q0, Q1, Q2, Q3, Q4, Q5, Q6, Q7, Q8, Q9, Q10, Q11, Q12, Q13, Q14, Q15]), "radius" : 2 * mm, "tangentPropagation" : true, "allowEdgeOverflow" : false});
        }
        {
            var Q0;
            Q0=makeQuery(id+"F9.opExtrude","CAP_FACE",FACE,{"disambiguationData":[OSD([sQuery(id+"F8.wireOp",EDGE,"E18.bottom"),sQuery(id+"F8.wireOp",EDGE,"E18.top"),sQuery(id+"F8.wireOp",EDGE,"E18.left"),sQuery(id+"F8.wireOp",EDGE,"E18.right")])],"isStart":false});
            var Q1;
            Q1=makeQuery(id+"F9.opExtrude","CAP_FACE",FACE,{"disambiguationData":[OSD([sQuery(id+"F8.wireOp",EDGE,"E19.3.0"),sQuery(id+"F8.wireOp",EDGE,"E19.3.1"),sQuery(id+"F8.wireOp",EDGE,"E19.3.2"),sQuery(id+"F8.wireOp",EDGE,"E19.3.3")])],"isStart":false});
            var Q2;
            Q2=makeQuery(id+"F9.opExtrude","CAP_FACE",FACE,{"disambiguationData":[OSD([sQuery(id+"F8.wireOp",EDGE,"E19.2.0"),sQuery(id+"F8.wireOp",EDGE,"E19.2.1"),sQuery(id+"F8.wireOp",EDGE,"E19.2.2"),sQuery(id+"F8.wireOp",EDGE,"E19.2.3")])],"isStart":false});
            var Q3;
            Q3=makeQuery(id+"F9.opExtrude","CAP_FACE",FACE,{"disambiguationData":[OSD([sQuery(id+"F8.wireOp",EDGE,"E19.1.0"),sQuery(id+"F8.wireOp",EDGE,"E19.1.1"),sQuery(id+"F8.wireOp",EDGE,"E19.1.2"),sQuery(id+"F8.wireOp",EDGE,"E19.1.3")])],"isStart":false});
            fillet(context, id + "F13", {"entities" : qUnion([Q0, Q1, Q2, Q3]), "radius" : 0.5 * mm, "tangentPropagation" : true, "allowEdgeOverflow" : false});
        }
        {
            var Q0;
            Q0=makeQuery(id+"F11.boolean.opBoolean","COPY",EDGE,{"derivedFrom":makeQuery(id+"F11.opExtrude","CAP_EDGE",EDGE,{"disambiguationData":[OSD([sQuery(id+"F10.wireOp",EDGE,"E24.1.0")])],"isStart":false})});
            var Q1;
            Q1=makeQuery(id+"F11.boolean.opBoolean","COPY",EDGE,{"derivedFrom":makeQuery(id+"F11.opExtrude","CAP_EDGE",EDGE,{"disambiguationData":[OSD([sQuery(id+"F10.wireOp",EDGE,"E23.bottom")])],"isStart":false})});
            var Q2;
            Q2=makeQuery(id+"F11.boolean.opBoolean","COPY",EDGE,{"derivedFrom":makeQuery(id+"F11.opExtrude","CAP_EDGE",EDGE,{"disambiguationData":[OSD([sQuery(id+"F10.wireOp",EDGE,"E24.3.1")])],"isStart":false})});
            var Q3;
            Q3=makeQuery(id+"F11.boolean.opBoolean","COPY",EDGE,{"derivedFrom":makeQuery(id+"F11.opExtrude","CAP_EDGE",EDGE,{"disambiguationData":[OSD([sQuery(id+"F10.wireOp",EDGE,"E24.2.0")])],"isStart":false})});
            var Q4;
            Q4=makeQuery(id+"F11.boolean.opBoolean","COPY",EDGE,{"derivedFrom":makeQuery(id+"F11.opExtrude","CAP_EDGE",EDGE,{"disambiguationData":[OSD([sQuery(id+"F10.wireOp",EDGE,"E24.2.1")])],"isStart":false})});
            var Q5;
            Q5=makeQuery(id+"F11.boolean.opBoolean","COPY",EDGE,{"derivedFrom":makeQuery(id+"F11.opExtrude","CAP_EDGE",EDGE,{"disambiguationData":[OSD([sQuery(id+"F10.wireOp",EDGE,"E24.3.0")])],"isStart":false})});
            var Q6;
            Q6=makeQuery(id+"F11.boolean.opBoolean","COPY",EDGE,{"derivedFrom":makeQuery(id+"F11.opExtrude","CAP_EDGE",EDGE,{"disambiguationData":[OSD([sQuery(id+"F10.wireOp",EDGE,"E24.1.1")])],"isStart":false})});
            var Q7;
            Q7=makeQuery(id+"F11.boolean.opBoolean","COPY",EDGE,{"derivedFrom":makeQuery(id+"F11.opExtrude","CAP_EDGE",EDGE,{"disambiguationData":[OSD([sQuery(id+"F10.wireOp",EDGE,"E23.top")])],"isStart":false})});
            var Q8;
            Q8=makeQuery(id+"F11.boolean.opBoolean","COPY",EDGE,{"derivedFrom":makeQuery(id+"F11.opExtrude","CAP_EDGE",EDGE,{"disambiguationData":[OSD([sQuery(id+"F10.wireOp",EDGE,"E24.2.0")])],"isStart":true})});
            var Q9;
            Q9=makeQuery(id+"F11.boolean.opBoolean","COPY",EDGE,{"derivedFrom":makeQuery(id+"F11.opExtrude","CAP_EDGE",EDGE,{"disambiguationData":[OSD([sQuery(id+"F10.wireOp",EDGE,"E24.1.0")])],"isStart":true})});
            var Q10;
            Q10=makeQuery(id+"F11.boolean.opBoolean","COPY",EDGE,{"derivedFrom":makeQuery(id+"F11.opExtrude","CAP_EDGE",EDGE,{"disambiguationData":[OSD([sQuery(id+"F10.wireOp",EDGE,"E23.top")])],"isStart":true})});
            var Q11;
            Q11=makeQuery(id+"F11.boolean.opBoolean","COPY",EDGE,{"derivedFrom":makeQuery(id+"F11.opExtrude","CAP_EDGE",EDGE,{"disambiguationData":[OSD([sQuery(id+"F10.wireOp",EDGE,"E24.3.1")])],"isStart":true})});
            var Q12;
            Q12=makeQuery(id+"F11.boolean.opBoolean","COPY",EDGE,{"derivedFrom":makeQuery(id+"F11.opExtrude","CAP_EDGE",EDGE,{"disambiguationData":[OSD([sQuery(id+"F10.wireOp",EDGE,"E24.3.0")])],"isStart":true})});
            var Q13;
            Q13=makeQuery(id+"F11.boolean.opBoolean","COPY",EDGE,{"derivedFrom":makeQuery(id+"F11.opExtrude","CAP_EDGE",EDGE,{"disambiguationData":[OSD([sQuery(id+"F10.wireOp",EDGE,"E24.1.1")])],"isStart":true})});
            var Q14;
            Q14=makeQuery(id+"F11.boolean.opBoolean","COPY",EDGE,{"derivedFrom":makeQuery(id+"F11.opExtrude","CAP_EDGE",EDGE,{"disambiguationData":[OSD([sQuery(id+"F10.wireOp",EDGE,"E23.bottom")])],"isStart":true})});
            var Q15;
            Q15=makeQuery(id+"F11.boolean.opBoolean","COPY",EDGE,{"derivedFrom":makeQuery(id+"F11.opExtrude","CAP_EDGE",EDGE,{"disambiguationData":[OSD([sQuery(id+"F10.wireOp",EDGE,"E24.2.1")])],"isStart":true})});
            fillet(context, id + "F14", {"entities" : qUnion([Q0, Q1, Q2, Q3, Q4, Q5, Q6, Q7, Q8, Q9, Q10, Q11, Q12, Q13, Q14, Q15]), "radius" : 1 * mm, "tangentPropagation" : true, "allowEdgeOverflow" : false});
        }
    });
